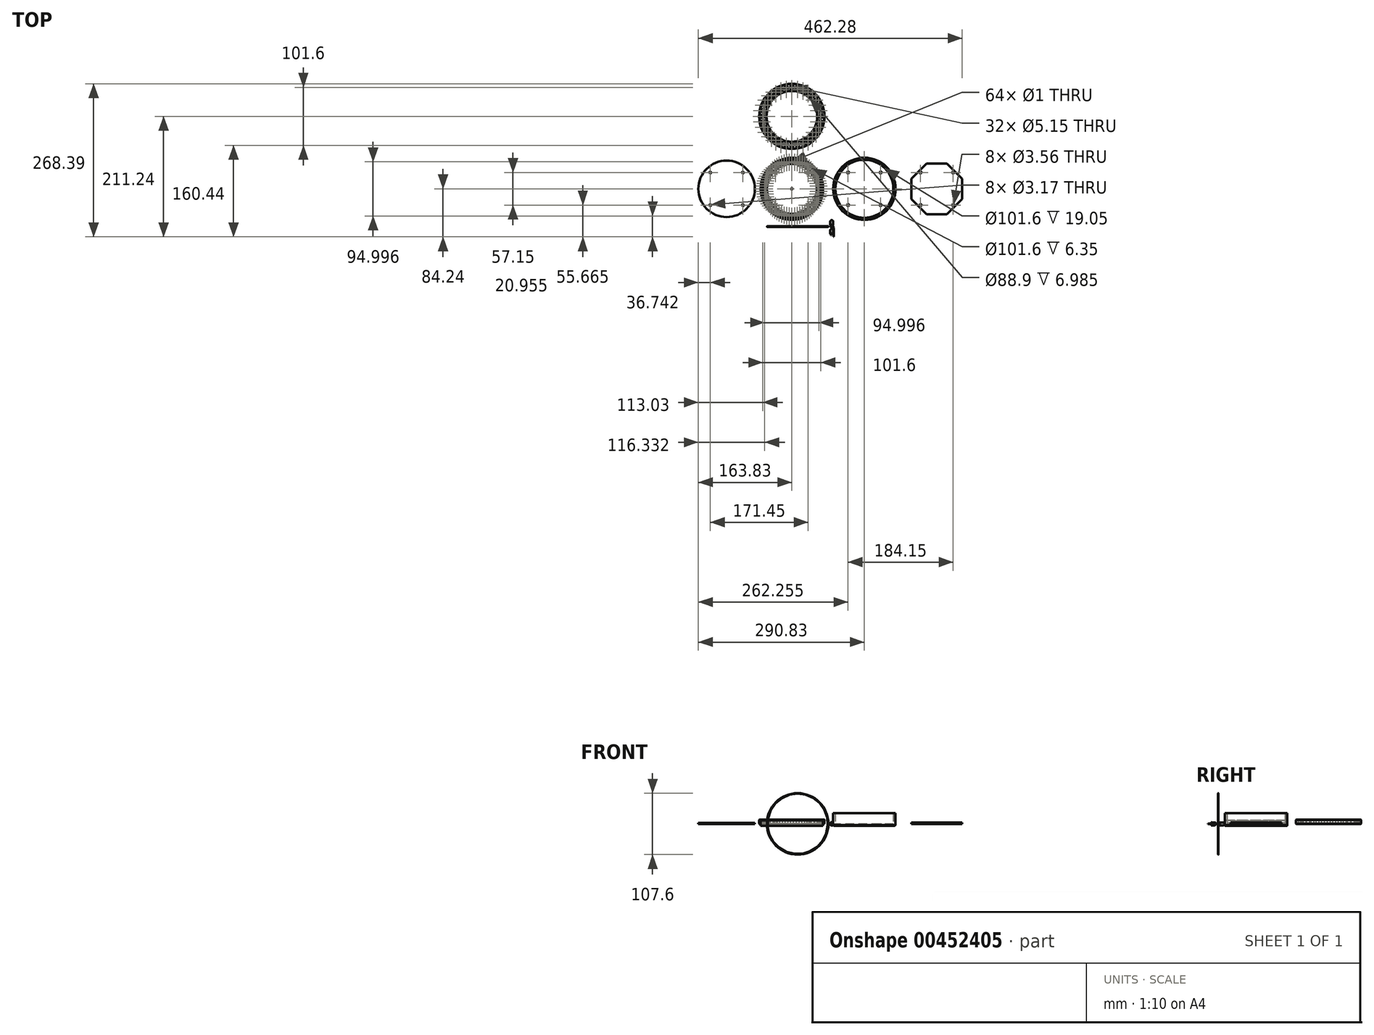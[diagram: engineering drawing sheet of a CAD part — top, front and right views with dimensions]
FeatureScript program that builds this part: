
annotation { "Feature Type Name" : "Feature", "Feature Type Description" : "" }
export const myFeature = defineFeature(function(context is Context, id is Id, definition is map)
    precondition{}
    {
        {
            var Q0;
            Q0=qCreatedBy(makeId("Top.planeOp"),FACE);
            var sketch = newSketch(context, id + "F0", { "sketchPlane" : qUnion([Q0])});
            skLineSegment(sketch, "E0.bottom", {"start": v(6.35, 0) * mm, "end": v(8.85, 0) * mm});
            skLineSegment(sketch, "E0.top", {"start": v(6.35, 6.1) * mm, "end": v(8.85, 6.1) * mm});
            skLineSegment(sketch, "E0.left", {"start": v(6.35, 0) * mm, "end": v(6.35, 6.1) * mm});
            skLineSegment(sketch, "E0.right", {"start": v(8.85, 0) * mm, "end": v(8.85, 6.1) * mm});
            skLineSegment(sketch, "E1.bottom", {"start": v(8.85, 0) * mm, "end": v(9.35, 0) * mm});
            skLineSegment(sketch, "E1.top", {"start": v(8.85, 0.5) * mm, "end": v(9.35, 0.5) * mm});
            skLineSegment(sketch, "E1.left", {"start": v(8.85, 0) * mm, "end": v(8.85, 0.5) * mm});
            skLineSegment(sketch, "E1.right", {"start": v(9.35, 0) * mm, "end": v(9.35, 0.5) * mm});
            skArc(sketch, "E2", {"start": v(8.85, 6.1) * mm, "mid": v(8.12, 7.87) * mm, "end": v(6.35, 8.6) * mm});
            skLineSegment(sketch, "E3", {"start": v(6.35, 6.1) * mm, "end": v(6.35, 8.6) * mm});
            skCircle(sketch, "E4", {"center": v(-63.5, 63.5) * mm, "radius": 54.61 * mm});
            skCircle(sketch, "E5", {"center": v(-63.5, 63.5) * mm, "radius": 1.27 * mm});
            skCircle(sketch, "E6", {"center": v(0, -2.54) * mm, "radius": 0.46 * mm});
            skLineSegment(sketch, "E7", {"start": v(-53.34, 0) * mm, "end": v(-53.34, -7.62) * mm});
            skCircle(sketch, "E8", {"center": v(-111, 63.5) * mm, "radius": 0.5 * mm});
            skCircle(sketch, "E9.1.0", {"center": v(-110.77, 58.84) * mm, "radius": 0.5 * mm});
            skCircle(sketch, "E9.2.0", {"center": v(-110.09, 54.23) * mm, "radius": 0.5 * mm});
            skCircle(sketch, "E9.3.0", {"center": v(-108.95, 49.71) * mm, "radius": 0.5 * mm});
            skCircle(sketch, "E9.4.0", {"center": v(-107.38, 45.32) * mm, "radius": 0.5 * mm});
            skCircle(sketch, "E9.5.0", {"center": v(-105.39, 41.1) * mm, "radius": 0.5 * mm});
            skCircle(sketch, "E9.6.0", {"center": v(-103, 37.11) * mm, "radius": 0.5 * mm});
            skCircle(sketch, "E9.7.0", {"center": v(-100.22, 33.37) * mm, "radius": 0.5 * mm});
            skCircle(sketch, "E9.8.0", {"center": v(-97.09, 29.91) * mm, "radius": 0.5 * mm});
            skCircle(sketch, "E9.9.0", {"center": v(-93.63, 26.78) * mm, "radius": 0.5 * mm});
            skCircle(sketch, "E9.10.0", {"center": v(-89.89, 24) * mm, "radius": 0.5 * mm});
            skCircle(sketch, "E9.11.0", {"center": v(-85.9, 21.61) * mm, "radius": 0.5 * mm});
            skCircle(sketch, "E9.12.0", {"center": v(-81.68, 19.62) * mm, "radius": 0.5 * mm});
            skCircle(sketch, "E9.13.0", {"center": v(-77.29, 18.05) * mm, "radius": 0.5 * mm});
            skCircle(sketch, "E9.14.0", {"center": v(-72.77, 16.91) * mm, "radius": 0.5 * mm});
            skCircle(sketch, "E9.15.0", {"center": v(-68.16, 16.23) * mm, "radius": 0.5 * mm});
            skCircle(sketch, "E9.16.0", {"center": v(-63.5, 16) * mm, "radius": 0.5 * mm});
            skCircle(sketch, "E9.17.0", {"center": v(-58.84, 16.23) * mm, "radius": 0.5 * mm});
            skCircle(sketch, "E9.18.0", {"center": v(-54.23, 16.91) * mm, "radius": 0.5 * mm});
            skCircle(sketch, "E9.19.0", {"center": v(-49.71, 18.05) * mm, "radius": 0.5 * mm});
            skCircle(sketch, "E9.20.0", {"center": v(-45.32, 19.62) * mm, "radius": 0.5 * mm});
            skCircle(sketch, "E9.21.0", {"center": v(-41.1, 21.61) * mm, "radius": 0.5 * mm});
            skCircle(sketch, "E9.22.0", {"center": v(-37.11, 24) * mm, "radius": 0.5 * mm});
            skCircle(sketch, "E9.23.0", {"center": v(-33.37, 26.78) * mm, "radius": 0.5 * mm});
            skCircle(sketch, "E9.24.0", {"center": v(-29.91, 29.91) * mm, "radius": 0.5 * mm});
            skCircle(sketch, "E9.25.0", {"center": v(-26.78, 33.37) * mm, "radius": 0.5 * mm});
            skCircle(sketch, "E9.26.0", {"center": v(-24, 37.11) * mm, "radius": 0.5 * mm});
            skCircle(sketch, "E9.27.0", {"center": v(-21.61, 41.1) * mm, "radius": 0.5 * mm});
            skCircle(sketch, "E9.28.0", {"center": v(-19.62, 45.32) * mm, "radius": 0.5 * mm});
            skCircle(sketch, "E9.29.0", {"center": v(-18.05, 49.71) * mm, "radius": 0.5 * mm});
            skCircle(sketch, "E9.30.0", {"center": v(-16.91, 54.23) * mm, "radius": 0.5 * mm});
            skCircle(sketch, "E9.31.0", {"center": v(-16.23, 58.84) * mm, "radius": 0.5 * mm});
            skCircle(sketch, "E10", {"center": v(-63.5, 63.5) * mm, "radius": 50.8 * mm});
            skCircle(sketch, "E11", {"center": v(-63.5, 63.5) * mm, "radius": 45.72 * mm});
            skCircle(sketch, "E12", {"center": v(-63.5, 63.5) * mm, "radius": 43.82 * mm});
            skCircle(sketch, "E13.1.32.0", {"center": v(-16, 63.5) * mm, "radius": 0.5 * mm});
            skCircle(sketch, "E13.1.33.0", {"center": v(-16.23, 68.16) * mm, "radius": 0.5 * mm});
            skCircle(sketch, "E13.1.34.0", {"center": v(-16.91, 72.77) * mm, "radius": 0.5 * mm});
            skCircle(sketch, "E13.1.35.0", {"center": v(-18.05, 77.29) * mm, "radius": 0.5 * mm});
            skCircle(sketch, "E13.1.36.0", {"center": v(-19.62, 81.68) * mm, "radius": 0.5 * mm});
            skCircle(sketch, "E13.1.37.0", {"center": v(-21.61, 85.9) * mm, "radius": 0.5 * mm});
            skCircle(sketch, "E13.1.38.0", {"center": v(-24, 89.89) * mm, "radius": 0.5 * mm});
            skCircle(sketch, "E13.1.39.0", {"center": v(-26.78, 93.63) * mm, "radius": 0.5 * mm});
            skCircle(sketch, "E13.1.40.0", {"center": v(-29.91, 97.09) * mm, "radius": 0.5 * mm});
            skCircle(sketch, "E13.1.41.0", {"center": v(-33.37, 100.22) * mm, "radius": 0.5 * mm});
            skCircle(sketch, "E13.1.42.0", {"center": v(-37.11, 103) * mm, "radius": 0.5 * mm});
            skCircle(sketch, "E13.1.43.0", {"center": v(-41.1, 105.39) * mm, "radius": 0.5 * mm});
            skCircle(sketch, "E13.1.44.0", {"center": v(-45.32, 107.38) * mm, "radius": 0.5 * mm});
            skCircle(sketch, "E13.1.45.0", {"center": v(-49.71, 108.95) * mm, "radius": 0.5 * mm});
            skCircle(sketch, "E13.1.46.0", {"center": v(-54.23, 110.09) * mm, "radius": 0.5 * mm});
            skCircle(sketch, "E13.1.47.0", {"center": v(-58.84, 110.77) * mm, "radius": 0.5 * mm});
            skCircle(sketch, "E13.1.48.0", {"center": v(-63.5, 111) * mm, "radius": 0.5 * mm});
            skCircle(sketch, "E13.1.49.0", {"center": v(-68.16, 110.77) * mm, "radius": 0.5 * mm});
            skCircle(sketch, "E13.1.50.0", {"center": v(-72.77, 110.09) * mm, "radius": 0.5 * mm});
            skCircle(sketch, "E13.1.51.0", {"center": v(-77.29, 108.95) * mm, "radius": 0.5 * mm});
            skCircle(sketch, "E13.1.52.0", {"center": v(-81.68, 107.38) * mm, "radius": 0.5 * mm});
            skCircle(sketch, "E13.1.53.0", {"center": v(-85.9, 105.39) * mm, "radius": 0.5 * mm});
            skCircle(sketch, "E13.1.54.0", {"center": v(-89.89, 103) * mm, "radius": 0.5 * mm});
            skCircle(sketch, "E13.1.55.0", {"center": v(-93.63, 100.22) * mm, "radius": 0.5 * mm});
            skCircle(sketch, "E13.1.56.0", {"center": v(-97.09, 97.09) * mm, "radius": 0.5 * mm});
            skCircle(sketch, "E13.1.57.0", {"center": v(-100.22, 93.63) * mm, "radius": 0.5 * mm});
            skCircle(sketch, "E13.1.58.0", {"center": v(-103, 89.89) * mm, "radius": 0.5 * mm});
            skCircle(sketch, "E13.1.59.0", {"center": v(-105.39, 85.9) * mm, "radius": 0.5 * mm});
            skCircle(sketch, "E13.1.60.0", {"center": v(-107.38, 81.68) * mm, "radius": 0.5 * mm});
            skCircle(sketch, "E13.1.61.0", {"center": v(-108.95, 77.29) * mm, "radius": 0.5 * mm});
            skCircle(sketch, "E13.1.62.0", {"center": v(-110.09, 72.77) * mm, "radius": 0.5 * mm});
            skCircle(sketch, "E13.1.63.0", {"center": v(-110.77, 68.16) * mm, "radius": 0.5 * mm});
            skLineSegment(sketch, "E14.bottom", {"start": v(-34.92, 92.07) * mm, "end": v(-92.08, 92.07) * mm, "construction": true});
            skLineSegment(sketch, "E14.top", {"start": v(-34.93, 34.92) * mm, "end": v(-92.08, 34.92) * mm, "construction": true});
            skLineSegment(sketch, "E14.left", {"start": v(-34.93, 92.08) * mm, "end": v(-34.93, 34.92) * mm, "construction": true});
            skLineSegment(sketch, "E14.right", {"start": v(-92.08, 92.08) * mm, "end": v(-92.08, 34.92) * mm, "construction": true});
            skCircle(sketch, "E15", {"center": v(-92.08, 92.08) * mm, "radius": 1.59 * mm});
            skCircle(sketch, "E16", {"center": v(-34.92, 92.08) * mm, "radius": 1.59 * mm});
            skCircle(sketch, "E17", {"center": v(-34.93, 34.92) * mm, "radius": 1.59 * mm});
            skCircle(sketch, "E18", {"center": v(-92.08, 34.92) * mm, "radius": 1.59 * mm});
            skCircle(sketch, "E19", {"center": v(63.5, 63.5) * mm, "radius": 54.61 * mm});
            skCircle(sketch, "E20", {"center": v(63.5, 63.5) * mm, "radius": 50.8 * mm});
            skLineSegment(sketch, "E21.bottom", {"start": v(34.92, 92.08) * mm, "end": v(92.08, 92.08) * mm, "construction": true});
            skLineSegment(sketch, "E21.top", {"start": v(34.92, 34.92) * mm, "end": v(92.08, 34.93) * mm, "construction": true});
            skLineSegment(sketch, "E21.left", {"start": v(34.93, 92.08) * mm, "end": v(34.93, 34.93) * mm, "construction": true});
            skLineSegment(sketch, "E21.right", {"start": v(92.08, 92.08) * mm, "end": v(92.08, 34.93) * mm, "construction": true});
            skCircle(sketch, "E22", {"center": v(34.92, 92.08) * mm, "radius": 1.78 * mm});
            skCircle(sketch, "E23", {"center": v(92.08, 92.08) * mm, "radius": 1.78 * mm});
            skCircle(sketch, "E24", {"center": v(92.08, 34.93) * mm, "radius": 1.78 * mm});
            skCircle(sketch, "E25", {"center": v(34.92, 34.93) * mm, "radius": 1.78 * mm});
            skPoint(sketch, "E26.cCircle.perimeterSnap0", {"position": v(92.08, 63.5) * mm});
            skPoint(sketch, "E26.0.midPoint.positionSnap0", {"position": v(92.08, 63.5) * mm});
            skLineSegment(sketch, "E27.bottom", {"start": v(146.05, 107.95) * mm, "end": v(234.95, 107.95) * mm});
            skLineSegment(sketch, "E27.top", {"start": v(146.05, 19.05) * mm, "end": v(234.95, 19.05) * mm});
            skLineSegment(sketch, "E27.left", {"start": v(146.05, 107.95) * mm, "end": v(146.05, 19.05) * mm});
            skLineSegment(sketch, "E27.right", {"start": v(234.95, 107.95) * mm, "end": v(234.95, 19.05) * mm});
            skPoint(sketch, "E27.middle", {"position": v(190.5, 63.5) * mm});
            skLineSegment(sketch, "E28.bottom", {"start": v(161.92, 92.08) * mm, "end": v(219.08, 92.08) * mm, "construction": true});
            skLineSegment(sketch, "E28.top", {"start": v(161.93, 34.93) * mm, "end": v(219.08, 34.93) * mm, "construction": true});
            skLineSegment(sketch, "E28.left", {"start": v(161.93, 92.08) * mm, "end": v(161.93, 34.93) * mm, "construction": true});
            skLineSegment(sketch, "E28.right", {"start": v(219.08, 92.08) * mm, "end": v(219.08, 34.93) * mm, "construction": true});
            skCircle(sketch, "E29", {"center": v(190.5, 63.5) * mm, "radius": 50.8 * mm, "construction": true});
            skLineSegment(sketch, "E30.bottom", {"start": v(234.95, 81.28) * mm, "end": v(146.05, 81.28) * mm, "construction": true});
            skLineSegment(sketch, "E30.top", {"start": v(234.95, 45.72) * mm, "end": v(146.05, 45.72) * mm, "construction": true});
            skLineSegment(sketch, "E30.left", {"start": v(234.95, 81.28) * mm, "end": v(234.95, 45.72) * mm, "construction": true});
            skLineSegment(sketch, "E30.right", {"start": v(146.05, 81.28) * mm, "end": v(146.05, 45.72) * mm, "construction": true});
            skLineSegment(sketch, "E31.bottom", {"start": v(208.28, 107.95) * mm, "end": v(172.72, 107.95) * mm, "construction": true});
            skLineSegment(sketch, "E31.top", {"start": v(208.28, 19.05) * mm, "end": v(172.72, 19.05) * mm, "construction": true});
            skLineSegment(sketch, "E31.left", {"start": v(208.28, 107.95) * mm, "end": v(208.28, 19.05) * mm, "construction": true});
            skLineSegment(sketch, "E31.right", {"start": v(172.72, 107.95) * mm, "end": v(172.72, 19.05) * mm, "construction": true});
            skLineSegment(sketch, "E32", {"start": v(146.05, 81.28) * mm, "end": v(172.72, 107.95) * mm});
            skLineSegment(sketch, "E33", {"start": v(146.05, 45.72) * mm, "end": v(172.72, 19.05) * mm});
            skLineSegment(sketch, "E34", {"start": v(208.28, 19.05) * mm, "end": v(234.95, 45.72) * mm});
            skLineSegment(sketch, "E35", {"start": v(234.95, 81.28) * mm, "end": v(208.28, 107.95) * mm});
            skCircle(sketch, "E36", {"center": v(161.92, 92.08) * mm, "radius": 1.78 * mm});
            skCircle(sketch, "E37", {"center": v(219.08, 92.08) * mm, "radius": 1.78 * mm});
            skCircle(sketch, "E38", {"center": v(219.08, 34.93) * mm, "radius": 1.78 * mm});
            skCircle(sketch, "E39", {"center": v(161.93, 34.93) * mm, "radius": 1.78 * mm});
            skCircle(sketch, "E40", {"center": v(-177.8, 63.5) * mm, "radius": 49.53 * mm});
            skLineSegment(sketch, "E41.bottom", {"start": v(-149.23, 92.08) * mm, "end": v(-206.38, 92.08) * mm, "construction": true});
            skLineSegment(sketch, "E41.top", {"start": v(-149.23, 34.92) * mm, "end": v(-206.38, 34.93) * mm, "construction": true});
            skLineSegment(sketch, "E41.left", {"start": v(-149.23, 92.08) * mm, "end": v(-149.23, 34.93) * mm, "construction": true});
            skLineSegment(sketch, "E41.right", {"start": v(-206.38, 92.08) * mm, "end": v(-206.38, 34.93) * mm, "construction": true});
            skCircle(sketch, "E42", {"center": v(-206.38, 92.08) * mm, "radius": 1.59 * mm});
            skCircle(sketch, "E43", {"center": v(-149.23, 92.08) * mm, "radius": 1.59 * mm});
            skCircle(sketch, "E44", {"center": v(-149.23, 34.92) * mm, "radius": 1.59 * mm});
            skCircle(sketch, "E45", {"center": v(-206.38, 34.93) * mm, "radius": 1.59 * mm});
            skCircle(sketch, "E46", {"center": v(-63.5, 190.5) * mm, "radius": 57.15 * mm});
            skCircle(sketch, "E47", {"center": v(-63.5, 190.5) * mm, "radius": 44.45 * mm});
            skCircle(sketch, "E48", {"center": v(-63.5, 190.5) * mm, "radius": 50.8 * mm, "construction": true});
            skCircle(sketch, "E49", {"center": v(-114.3, 190.5) * mm, "radius": 2.58 * mm});
            skCircle(sketch, "E50.1.0", {"center": v(-113.32, 180.59) * mm, "radius": 2.58 * mm});
            skCircle(sketch, "E50.2.0", {"center": v(-110.43, 171.06) * mm, "radius": 2.58 * mm});
            skCircle(sketch, "E50.3.0", {"center": v(-105.74, 162.28) * mm, "radius": 2.58 * mm});
            skCircle(sketch, "E50.4.0", {"center": v(-99.42, 154.58) * mm, "radius": 2.58 * mm});
            skCircle(sketch, "E50.5.0", {"center": v(-91.72, 148.26) * mm, "radius": 2.58 * mm});
            skCircle(sketch, "E50.6.0", {"center": v(-82.94, 143.57) * mm, "radius": 2.58 * mm});
            skCircle(sketch, "E50.7.0", {"center": v(-73.41, 140.68) * mm, "radius": 2.58 * mm});
            skCircle(sketch, "E50.8.0", {"center": v(-63.5, 139.7) * mm, "radius": 2.58 * mm});
            skCircle(sketch, "E50.9.0", {"center": v(-53.59, 140.68) * mm, "radius": 2.58 * mm});
            skCircle(sketch, "E50.10.0", {"center": v(-44.06, 143.57) * mm, "radius": 2.58 * mm});
            skCircle(sketch, "E50.11.0", {"center": v(-35.28, 148.26) * mm, "radius": 2.58 * mm});
            skCircle(sketch, "E50.12.0", {"center": v(-27.58, 154.58) * mm, "radius": 2.58 * mm});
            skCircle(sketch, "E50.13.0", {"center": v(-21.26, 162.28) * mm, "radius": 2.58 * mm});
            skCircle(sketch, "E50.14.0", {"center": v(-16.57, 171.06) * mm, "radius": 2.58 * mm});
            skCircle(sketch, "E50.15.0", {"center": v(-13.68, 180.59) * mm, "radius": 2.58 * mm});
            skCircle(sketch, "E50.16.0", {"center": v(-12.7, 190.5) * mm, "radius": 2.58 * mm});
            skCircle(sketch, "E50.17.0", {"center": v(-13.68, 200.41) * mm, "radius": 2.58 * mm});
            skCircle(sketch, "E50.18.0", {"center": v(-16.57, 209.94) * mm, "radius": 2.58 * mm});
            skCircle(sketch, "E50.19.0", {"center": v(-21.26, 218.72) * mm, "radius": 2.58 * mm});
            skCircle(sketch, "E50.20.0", {"center": v(-27.58, 226.42) * mm, "radius": 2.58 * mm});
            skCircle(sketch, "E50.21.0", {"center": v(-35.28, 232.74) * mm, "radius": 2.58 * mm});
            skCircle(sketch, "E50.22.0", {"center": v(-44.06, 237.43) * mm, "radius": 2.58 * mm});
            skCircle(sketch, "E50.23.0", {"center": v(-53.59, 240.32) * mm, "radius": 2.58 * mm});
            skCircle(sketch, "E50.24.0", {"center": v(-63.5, 241.3) * mm, "radius": 2.58 * mm});
            skCircle(sketch, "E50.25.0", {"center": v(-73.41, 240.32) * mm, "radius": 2.58 * mm});
            skCircle(sketch, "E50.26.0", {"center": v(-82.94, 237.43) * mm, "radius": 2.58 * mm});
            skCircle(sketch, "E50.27.0", {"center": v(-91.72, 232.74) * mm, "radius": 2.58 * mm});
            skCircle(sketch, "E50.28.0", {"center": v(-99.42, 226.42) * mm, "radius": 2.58 * mm});
            skCircle(sketch, "E50.29.0", {"center": v(-105.74, 218.72) * mm, "radius": 2.58 * mm});
            skCircle(sketch, "E50.30.0", {"center": v(-110.43, 209.94) * mm, "radius": 2.58 * mm});
            skCircle(sketch, "E50.31.0", {"center": v(-113.32, 200.41) * mm, "radius": 2.58 * mm});
            skSolve(sketch);
        }
        {
            var Q0;
            Q0=makeQuery(id+"F0.imprint","IMPRINT",FACE,{"disambiguationData":[TD([[makeQuery(id+"F0.imprint","IMPRINT",EDGE,{"derivedFrom":sQuery(id+"F0.wireOp",EDGE,"E1.bottom")}),1.0]])]});
            var Q1;
            Q1=makeQuery(id+"F0.imprint","IMPRINT",FACE,{"disambiguationData":[TD([[makeQuery(id+"F0.imprint","IMPRINT",EDGE,{"derivedFrom":sQuery(id+"F0.wireOp",EDGE,"E0.bottom")}),1.0]])]});
            var Q2;
            Q2=makeQuery(id+"F0.imprint","IMPRINT",FACE,{"disambiguationData":[TD([[makeQuery(id+"F0.imprint","IMPRINT",EDGE,{"derivedFrom":sQuery(id+"F0.wireOp",EDGE,"E0.top")}),1.0]])]});
            var Q3;
            Q3=sQuery(id+"F0.wireOp",EDGE,"E0.left");
            revolve(context, id + "F1", {"entities" : qUnion([Q0, Q1, Q2]), "axis" : qUnion([Q3]), "revolveType" : RevolveType.FULL});
        }
        {
            var Q0;
            Q0=makeQuery(id+"F1.opRevolve","SWEPT_FACE",FACE,{"disambiguationData":[OSD([sQuery(id+"F0.wireOp",EDGE,"E0.bottom"),sQuery(id+"F0.wireOp",EDGE,"E1.bottom")])]});
            var sketch = newSketch(context, id + "F2", { "sketchPlane" : qUnion([Q0])});
            skLineSegment(sketch, "E51.bottom", {"start": v(5.38, 0.3) * mm, "end": v(4.78, 0.3) * mm});
            skLineSegment(sketch, "E51.top", {"start": v(5.38, -0.3) * mm, "end": v(4.78, -0.3) * mm});
            skLineSegment(sketch, "E51.left", {"start": v(5.38, 0.3) * mm, "end": v(5.38, -0.3) * mm});
            skLineSegment(sketch, "E51.right", {"start": v(4.78, 0.3) * mm, "end": v(4.78, -0.3) * mm});
            skPoint(sketch, "E51.middle", {"position": v(5.08, 0) * mm});
            skLineSegment(sketch, "E52.bottom", {"start": v(7.92, 0.3) * mm, "end": v(7.32, 0.3) * mm});
            skLineSegment(sketch, "E52.top", {"start": v(7.92, -0.3) * mm, "end": v(7.32, -0.3) * mm});
            skLineSegment(sketch, "E52.left", {"start": v(7.92, 0.3) * mm, "end": v(7.92, -0.3) * mm});
            skLineSegment(sketch, "E52.right", {"start": v(7.32, 0.3) * mm, "end": v(7.32, -0.3) * mm});
            skPoint(sketch, "E52.middle", {"position": v(7.62, 0) * mm});
            skLineSegment(sketch, "E53", {"start": v(8.85, 1.66) * mm, "end": v(8.85, -1.66) * mm});
            skLineSegment(sketch, "E54", {"start": v(5.08, 0) * mm, "end": v(7.62, 0) * mm, "construction": true});
            skPoint(sketch, "E55", {"position": v(6.35, 0) * mm});
            skArc(sketch, "E56", {"start": v(8.85, 1.66) * mm, "mid": v(9.35, 0) * mm, "end": v(8.85, -1.66) * mm});
            skSolve(sketch);
        }
        {
            var Q0;
            Q0=makeQuery(id+"F2.imprint","IMPRINT",FACE,{"disambiguationData":[TD([[makeQuery(id+"F2.imprint","IMPRINT",EDGE,{"derivedFrom":sQuery(id+"F2.wireOp",EDGE,"E53")}),1.0]])]});
            var Q1;
            Q1=makeQuery(id+"F1.opRevolve","SWEPT_FACE",FACE,{"disambiguationData":[OSD([sQuery(id+"F0.wireOp",EDGE,"E1.top")])]});
            extrude(context, id + "F3", {"entities" : qUnion([Q0]), "operationType" : NewBodyOperationType.REMOVE, "endBound" : BoundingType.UP_TO_SURFACE, "oppositeDirection" : true, "endBoundEntityFace" : qUnion([Q1]), "depth" : 25.4 * mm});
        }
        {
            var Q0;
            Q0=makeQuery(id+"F2.imprint","IMPRINT",FACE,{"disambiguationData":[TD([[makeQuery(id+"F2.imprint","IMPRINT",EDGE,{"derivedFrom":sQuery(id+"F2.wireOp",EDGE,"E52.bottom")}),1.0]])]});
            extrude(context, id + "F4", {"entities" : qUnion([Q0]), "operationType" : NewBodyOperationType.ADD, "depth" : 1.9 * mm});
        }
        {
            var Q0;
            Q0=makeQuery(id+"F2.imprint","IMPRINT",FACE,{"disambiguationData":[TD([[makeQuery(id+"F2.imprint","IMPRINT",EDGE,{"derivedFrom":sQuery(id+"F2.wireOp",EDGE,"E51.bottom")}),1.0]])]});
            extrude(context, id + "F5", {"entities" : qUnion([Q0]), "operationType" : NewBodyOperationType.ADD, "depth" : 2.54 * mm});
        }
        {
            var Q0;
            Q0=makeQuery(id+"F0.imprint","IMPRINT",FACE,{"disambiguationData":[TD([[makeQuery(id+"F0.imprint","IMPRINT",EDGE,{"derivedFrom":sQuery(id+"F0.wireOp",EDGE,"E4")}),1.0]])]});
            var Q1;
            Q1=makeQuery(id+"F0.imprint","IMPRINT",FACE,{"disambiguationData":[TD([[makeQuery(id+"F0.imprint","IMPRINT",EDGE,{"derivedFrom":sQuery(id+"F0.wireOp",EDGE,"E5")}),1.0]])]});
            var Q2;
            Q2=makeQuery(id+"F0.imprint","IMPRINT",FACE,{"disambiguationData":[TD([[makeQuery(id+"F0.imprint","IMPRINT",EDGE,{"derivedFrom":sQuery(id+"F0.wireOp",EDGE,"E5")}),-1.0]])]});
            var Q3;
            Q3=makeQuery(id+"F0.imprint","IMPRINT",FACE,{"disambiguationData":[TD([[makeQuery(id+"F0.imprint","IMPRINT",EDGE,{"derivedFrom":sQuery(id+"F0.wireOp",EDGE,"E11")}),1.0]])]});
            var Q4;
            Q4=makeQuery(id+"F0.imprint","IMPRINT",FACE,{"disambiguationData":[TD([[makeQuery(id+"F0.imprint","IMPRINT",EDGE,{"derivedFrom":sQuery(id+"F0.wireOp",EDGE,"E8")}),-1.0]])]});
            extrude(context, id + "F6", {"entities" : qUnion([Q0, Q1, Q2, Q3, Q4]), "oppositeDirection" : true, "depth" : 3.17 * mm});
        }
        {
            var Q0;
            Q0=makeQuery(id+"F0.imprint","IMPRINT",FACE,{"disambiguationData":[TD([[makeQuery(id+"F0.imprint","IMPRINT",EDGE,{"derivedFrom":sQuery(id+"F0.wireOp",EDGE,"E5")}),1.0]])]});
            extrude(context, id + "F7", {"entities" : qUnion([Q0]), "operationType" : NewBodyOperationType.ADD, "depth" : 6.35 * mm});
        }
        {
            var Q0;
            Q0=makeQuery(id+"F1.opRevolve","SWEPT_BODY",BODY,{"disambiguationData":[OSD([sQuery(id+"F0.wireOp",EDGE,"E0.bottom"),sQuery(id+"F0.wireOp",EDGE,"E0.left"),sQuery(id+"F0.wireOp",EDGE,"E0.right"),sQuery(id+"F0.wireOp",EDGE,"E1.bottom"),sQuery(id+"F0.wireOp",EDGE,"E1.top"),sQuery(id+"F0.wireOp",EDGE,"E1.right"),sQuery(id+"F0.wireOp",EDGE,"E2"),sQuery(id+"F0.wireOp",EDGE,"E3")])]});
            transform(context, id + "F8", {"entities" : qUnion([Q0]), "transformType" : TransformType.TRANSLATION_3D, "dx" : 0 * mm, "dy" : -15.24 * mm, "dz" : 0 * mm, "makeCopy" : true});
        }
        {
            var Q0;
            Q0=makeQuery(id+"F4.opExtrude","CAP_FACE",FACE,{"disambiguationData":[OSD([sQuery(id+"F2.wireOp",EDGE,"E52.bottom"),sQuery(id+"F2.wireOp",EDGE,"E52.top"),sQuery(id+"F2.wireOp",EDGE,"E52.left"),sQuery(id+"F2.wireOp",EDGE,"E52.right")])],"isStart":false});
            var Q1;
            Q1=makeQuery(id+"F4.opExtrude","CAP_EDGE",EDGE,{"disambiguationData":[OSD([sQuery(id+"F2.wireOp",EDGE,"E52.left")])],"isStart":false});
            revolve(context, id + "F9", {"operationType" : NewBodyOperationType.ADD, "entities" : qUnion([Q0]), "axis" : qUnion([Q1]), "revolveType" : RevolveType.ONE_DIRECTION, "oppositeDirection" : true, "angle" : 30 * degree});
        }
        {
            var Q0;
            Q0=makeQuery(id+"F9.opRevolve","CAP_FACE",FACE,{"disambiguationData":[OSD([sQuery(id+"F2.wireOp",EDGE,"E52.bottom"),sQuery(id+"F2.wireOp",EDGE,"E52.top"),sQuery(id+"F2.wireOp",EDGE,"E52.left"),sQuery(id+"F2.wireOp",EDGE,"E52.right")])],"isStart":false});
            extrude(context, id + "F10", {"entities" : qUnion([Q0]), "operationType" : NewBodyOperationType.ADD, "depth" : 3.8 * mm});
        }
        {
            var Q0;
            Q0=makeQuery(id+"F10.opExtrude","CAP_FACE",FACE,{"disambiguationData":[OSD([sQuery(id+"F2.wireOp",EDGE,"E52.bottom"),sQuery(id+"F2.wireOp",EDGE,"E52.top"),sQuery(id+"F2.wireOp",EDGE,"E52.left"),sQuery(id+"F2.wireOp",EDGE,"E52.right")])],"isStart":false});
            var Q1;
            Q1=makeQuery(id+"F10.opExtrude","CAP_EDGE",EDGE,{"disambiguationData":[OSD([sQuery(id+"F2.wireOp",EDGE,"E52.right")])],"isStart":false});
            revolve(context, id + "F11", {"operationType" : NewBodyOperationType.ADD, "entities" : qUnion([Q0]), "axis" : qUnion([Q1]), "revolveType" : RevolveType.ONE_DIRECTION, "angle" : 30 * degree});
        }
        {
            var Q0;
            Q0=makeQuery(id+"F11.opRevolve","CAP_FACE",FACE,{"disambiguationData":[OSD([sQuery(id+"F2.wireOp",EDGE,"E52.bottom"),sQuery(id+"F2.wireOp",EDGE,"E52.top"),sQuery(id+"F2.wireOp",EDGE,"E52.left"),sQuery(id+"F2.wireOp",EDGE,"E52.right")])],"isStart":false});
            extrude(context, id + "F12", {"entities" : qUnion([Q0]), "operationType" : NewBodyOperationType.ADD, "depth" : 15.24 * mm});
        }
        {
            var Q0;
            Q0=makeQuery(id+"F5.opExtrude","CAP_FACE",FACE,{"disambiguationData":[OSD([sQuery(id+"F2.wireOp",EDGE,"E51.bottom"),sQuery(id+"F2.wireOp",EDGE,"E51.top"),sQuery(id+"F2.wireOp",EDGE,"E51.left"),sQuery(id+"F2.wireOp",EDGE,"E51.right")])],"isStart":false});
            var Q1;
            Q1=makeQuery(id+"F5.opExtrude","CAP_EDGE",EDGE,{"disambiguationData":[OSD([sQuery(id+"F2.wireOp",EDGE,"E51.right")])],"isStart":false});
            revolve(context, id + "F13", {"operationType" : NewBodyOperationType.ADD, "entities" : qUnion([Q0]), "axis" : qUnion([Q1]), "revolveType" : RevolveType.ONE_DIRECTION, "angle" : 89 * degree});
        }
        {
            var Q0;
            Q0=makeQuery(id+"F13.opRevolve","CAP_FACE",FACE,{"disambiguationData":[OSD([sQuery(id+"F2.wireOp",EDGE,"E51.bottom"),sQuery(id+"F2.wireOp",EDGE,"E51.top"),sQuery(id+"F2.wireOp",EDGE,"E51.left"),sQuery(id+"F2.wireOp",EDGE,"E51.right")])],"isStart":false});
            extrude(context, id + "F14", {"entities" : qUnion([Q0]), "operationType" : NewBodyOperationType.ADD, "depth" : 1.27 * mm});
        }
        {
            var Q0;
            Q0=makeQuery(id+"F0.imprint","IMPRINT",FACE,{"disambiguationData":[TD([[makeQuery(id+"F0.imprint","IMPRINT",EDGE,{"derivedFrom":sQuery(id+"F0.wireOp",EDGE,"E6")}),1.0]])]});
            var Q1;
            Q1=sQuery(id+"F0.wireOp",EDGE,"E7");
            revolve(context, id + "F15", {"entities" : qUnion([Q0]), "axis" : qUnion([Q1]), "revolveType" : RevolveType.FULL});
        }
        {
            var Q0;
            Q0=makeQuery(id+"F0.imprint","IMPRINT",FACE,{"disambiguationData":[TD([[makeQuery(id+"F0.imprint","IMPRINT",EDGE,{"derivedFrom":sQuery(id+"F0.wireOp",EDGE,"E4")}),1.0]])]});
            extrude(context, id + "F16", {"entities" : qUnion([Q0]), "operationType" : NewBodyOperationType.ADD, "depth" : 6.35 * mm});
        }
        {
            var Q0;
            Q0=makeQuery(id+"F0.imprint","IMPRINT",FACE,{"disambiguationData":[TD([[makeQuery(id+"F0.imprint","IMPRINT",EDGE,{"derivedFrom":sQuery(id+"F0.wireOp",EDGE,"E5")}),-1.0]])]});
            extrude(context, id + "F17", {"entities" : qUnion([Q0]), "operationType" : NewBodyOperationType.ADD, "depth" : 5.08 * mm});
        }
        {
            var Q0;
            Q0=makeQuery(id+"F0.imprint","IMPRINT",FACE,{"disambiguationData":[TD([[makeQuery(id+"F0.imprint","IMPRINT",EDGE,{"derivedFrom":sQuery(id+"F0.wireOp",EDGE,"E19")}),1.0]])]});
            var Q1;
            Q1=makeQuery(id+"F0.imprint","IMPRINT",FACE,{"disambiguationData":[TD([[makeQuery(id+"F0.imprint","IMPRINT",EDGE,{"derivedFrom":sQuery(id+"F0.wireOp",EDGE,"E20")}),1.0]])]});
            extrude(context, id + "F18", {"entities" : qUnion([Q0, Q1]), "oppositeDirection" : true, "depth" : 3.17 * mm});
        }
        {
            var Q0;
            Q0=makeQuery(id+"F0.imprint","IMPRINT",FACE,{"disambiguationData":[TD([[makeQuery(id+"F0.imprint","IMPRINT",EDGE,{"derivedFrom":sQuery(id+"F0.wireOp",EDGE,"E19")}),1.0]])]});
            extrude(context, id + "F19", {"entities" : qUnion([Q0]), "operationType" : NewBodyOperationType.ADD, "depth" : 19.05 * mm});
        }
        {
            var Q0;
            Q0=makeQuery(id+"F19.opExtrude","CAP_EDGE",EDGE,{"disambiguationData":[OSD([sQuery(id+"F0.wireOp",EDGE,"E20")])],"isStart":true});
            var Q1;
            Q1=makeQuery(id+"F18.opExtrude","CAP_EDGE",EDGE,{"disambiguationData":[OSD([sQuery(id+"F0.wireOp",EDGE,"E19")])],"isStart":false});
            chamfer(context, id + "F20", {"entities" : qUnion([Q0, Q1]), "width" : 1.27 * mm, "tangentPropagation" : true});
        }
        {
            var Q0;
            {var subQ2=sQuery(id+"F0.wireOp",EDGE,"E32");Q0=makeQuery(id+"F0.imprint","IMPRINT",FACE,{"disambiguationData":[TD([[makeQuery(id+"F0.imprint","IMPRINT",EDGE,{"derivedFrom":subQ2}),-1.0]])]});}
            extrude(context, id + "F21", {"entities" : qUnion([Q0]), "depth" : 2.36 * mm});
        }
        {
            var Q0;
            Q0=makeQuery(id+"F0.imprint","IMPRINT",FACE,{"disambiguationData":[TD([[makeQuery(id+"F0.imprint","IMPRINT",EDGE,{"derivedFrom":sQuery(id+"F0.wireOp",EDGE,"E40")}),1.0]])]});
            extrude(context, id + "F22", {"entities" : qUnion([Q0]), "depth" : 1.6 * mm});
        }
        {
            var Q0;
            Q0=makeQuery(id+"F0.imprint","IMPRINT",FACE,{"disambiguationData":[TD([[makeQuery(id+"F0.imprint","IMPRINT",EDGE,{"derivedFrom":sQuery(id+"F0.wireOp",EDGE,"E46")}),1.0]])]});
            extrude(context, id + "F23", {"entities" : qUnion([Q0]), "depth" : 7.62 * mm, "offsetDistance" : 25.4 * mm});
        }
        {
            var Q0;
            Q0=makeQuery(id+"F0.imprint","IMPRINT",FACE,{"disambiguationData":[TD([[makeQuery(id+"F0.imprint","IMPRINT",EDGE,{"derivedFrom":sQuery(id+"F0.wireOp",EDGE,"E47")}),1.0]])]});
            extrude(context, id + "F24", {"entities" : qUnion([Q0]), "operationType" : NewBodyOperationType.ADD, "depth" : 2.54 * mm, "offsetDistance" : 25.4 * mm});
        }
        {
            var Q0;
            Q0=makeQuery(id+"F23.opExtrude","CAP_FACE",FACE,{"disambiguationData":[OSD([sQuery(id+"F0.wireOp",EDGE,"E46"),sQuery(id+"F0.wireOp",EDGE,"E47"),sQuery(id+"F0.wireOp",EDGE,"E49"),sQuery(id+"F0.wireOp",EDGE,"E50.1.0"),sQuery(id+"F0.wireOp",EDGE,"E50.2.0"),sQuery(id+"F0.wireOp",EDGE,"E50.3.0"),sQuery(id+"F0.wireOp",EDGE,"E50.4.0"),sQuery(id+"F0.wireOp",EDGE,"E50.5.0"),sQuery(id+"F0.wireOp",EDGE,"E50.6.0"),sQuery(id+"F0.wireOp",EDGE,"E50.7.0"),sQuery(id+"F0.wireOp",EDGE,"E50.8.0"),sQuery(id+"F0.wireOp",EDGE,"E50.9.0"),sQuery(id+"F0.wireOp",EDGE,"E50.10.0"),sQuery(id+"F0.wireOp",EDGE,"E50.11.0"),sQuery(id+"F0.wireOp",EDGE,"E50.12.0"),sQuery(id+"F0.wireOp",EDGE,"E50.13.0"),sQuery(id+"F0.wireOp",EDGE,"E50.14.0"),sQuery(id+"F0.wireOp",EDGE,"E50.15.0"),sQuery(id+"F0.wireOp",EDGE,"E50.16.0"),sQuery(id+"F0.wireOp",EDGE,"E50.17.0"),sQuery(id+"F0.wireOp",EDGE,"E50.18.0"),sQuery(id+"F0.wireOp",EDGE,"E50.19.0"),sQuery(id+"F0.wireOp",EDGE,"E50.20.0"),sQuery(id+"F0.wireOp",EDGE,"E50.21.0"),sQuery(id+"F0.wireOp",EDGE,"E50.22.0"),sQuery(id+"F0.wireOp",EDGE,"E50.23.0"),sQuery(id+"F0.wireOp",EDGE,"E50.24.0"),sQuery(id+"F0.wireOp",EDGE,"E50.25.0"),sQuery(id+"F0.wireOp",EDGE,"E50.26.0"),sQuery(id+"F0.wireOp",EDGE,"E50.27.0"),sQuery(id+"F0.wireOp",EDGE,"E50.28.0"),sQuery(id+"F0.wireOp",EDGE,"E50.29.0"),sQuery(id+"F0.wireOp",EDGE,"E50.30.0"),sQuery(id+"F0.wireOp",EDGE,"E50.31.0")])],"isStart":false});
            var Q1;
            {var subQ0=sQuery(id+"F0.wireOp",EDGE,"E47");Q1=makeQuery(id+"F24.boolean.opBoolean","MERGE",FACE,{"derivedFrom":[makeQuery(id+"F23.opExtrude","CAP_FACE",FACE,{"disambiguationData":[OSD([sQuery(id+"F0.wireOp",EDGE,"E46"),subQ0,sQuery(id+"F0.wireOp",EDGE,"E49"),sQuery(id+"F0.wireOp",EDGE,"E50.1.0"),sQuery(id+"F0.wireOp",EDGE,"E50.2.0"),sQuery(id+"F0.wireOp",EDGE,"E50.3.0"),sQuery(id+"F0.wireOp",EDGE,"E50.4.0"),sQuery(id+"F0.wireOp",EDGE,"E50.5.0"),sQuery(id+"F0.wireOp",EDGE,"E50.6.0"),sQuery(id+"F0.wireOp",EDGE,"E50.7.0"),sQuery(id+"F0.wireOp",EDGE,"E50.8.0"),sQuery(id+"F0.wireOp",EDGE,"E50.9.0"),sQuery(id+"F0.wireOp",EDGE,"E50.10.0"),sQuery(id+"F0.wireOp",EDGE,"E50.11.0"),sQuery(id+"F0.wireOp",EDGE,"E50.12.0"),sQuery(id+"F0.wireOp",EDGE,"E50.13.0"),sQuery(id+"F0.wireOp",EDGE,"E50.14.0"),sQuery(id+"F0.wireOp",EDGE,"E50.15.0"),sQuery(id+"F0.wireOp",EDGE,"E50.16.0"),sQuery(id+"F0.wireOp",EDGE,"E50.17.0"),sQuery(id+"F0.wireOp",EDGE,"E50.18.0"),sQuery(id+"F0.wireOp",EDGE,"E50.19.0"),sQuery(id+"F0.wireOp",EDGE,"E50.20.0"),sQuery(id+"F0.wireOp",EDGE,"E50.21.0"),sQuery(id+"F0.wireOp",EDGE,"E50.22.0"),sQuery(id+"F0.wireOp",EDGE,"E50.23.0"),sQuery(id+"F0.wireOp",EDGE,"E50.24.0"),sQuery(id+"F0.wireOp",EDGE,"E50.25.0"),sQuery(id+"F0.wireOp",EDGE,"E50.26.0"),sQuery(id+"F0.wireOp",EDGE,"E50.27.0"),sQuery(id+"F0.wireOp",EDGE,"E50.28.0"),sQuery(id+"F0.wireOp",EDGE,"E50.29.0"),sQuery(id+"F0.wireOp",EDGE,"E50.30.0"),sQuery(id+"F0.wireOp",EDGE,"E50.31.0")])],"isStart":true}),makeQuery(id+"F24.opExtrude","CAP_FACE",FACE,{"disambiguationData":[OSD([subQ0])],"isStart":true})]});}
            chamfer(context, id + "F25", {"entities" : qUnion([Q0, Q1]), "width" : 0.64 * mm, "tangentPropagation" : true});
        }
        {
            var Q0;
            Q0=makeQuery(id+"F24.opExtrude","CAP_FACE",FACE,{"disambiguationData":[OSD([sQuery(id+"F0.wireOp",EDGE,"E47")])],"isStart":false});
            extrude(context, id + "F26", {"entities" : qUnion([Q0]), "operationType" : NewBodyOperationType.REMOVE, "endBound" : BoundingType.THROUGH_ALL, "oppositeDirection" : true, "depth" : 23.1 * mm, "offsetDistance" : 25.4 * mm});
        }
    });
